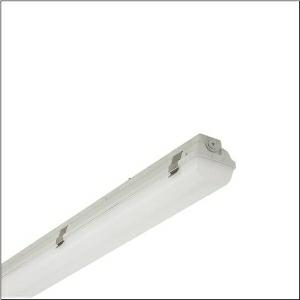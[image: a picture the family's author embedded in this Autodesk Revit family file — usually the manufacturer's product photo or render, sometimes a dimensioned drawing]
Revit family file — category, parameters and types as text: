
# Revit family: monsun_r__21_eco_51fj10dl45a_5ac6
name_source: partatom
category: Lighting Fixtures
units: mm (PartAtom-declared; Revit-internal decimal feet)

## family parameters
Cut with Voids When Loaded = No
Host = Face
Light Source = No
Part Type = Normal
Room Calculation Point = No
Round Connector Dimension = Use Diameter
Shared = No

## types (1)
- Monsun® 21 Eco (1 x LED, 5100 lm, 36 W, 4000K)
    Apparent Load = 36 VA
    CIE Flux Codes = 41 70 89 90 100
    Color Rendering = 80
    Color Temperature = 4000K
    Default Elevation = 1800 mm
    Description = Monsun® 21 Eco, damp-proof luminaire, primary optical cover: diffuser, of PMMA, frosted, light emission: direct distribution, primary light characteristic: symmetric, installation type: suspended mounting, surface-mounted, LED, rated luminous flux: 5.100lm, luminous efficacy: 142lm/W, light colour: 840, colour temperature: 4000K, control gear: ECG DALI, with terminal, 5-pole, max. 2.5mm², mains connection: 220..240V, AC, 50/60Hz, rated input power: 36W, housing, of glass-fibre reinforced polyester, light grey (RAL 7035), length: 1.277mm, width: 90mm, height: 95mm, clip for enclosure, of spring steel V2A, protection rating (complete): IP66, insulation class (complete): insulation class I (protective earthing), certification: CE, UKCA, protection symbol: D, impact resistance: IK02, permissible operating ambient temperature: -20..+35°C, corresponds to IFS (International Featured Standards) requirements for safety and quality in the food industry, packaging unit: 1 piece
    Height = 103 mm
    Lamp = 1 x LED
    Lamp Light Flux = 5100 lm
    Lamp Power = 36 W
    Lamp count = 1
    Length = 1277 mm
    Luminous efficacy = 142 lm/W
    Manufacturer = Siteco
    ModVariant = No
    Model = 51FJ10DL45A
    Mounting Place = Ceiling
    Mounting Type = Surface mounted
    Number of Poles = 1
    OnlyDefault = Yes
    Power Factor = 1
    Product Name = Monsun® 21 Eco
    Product group = damp-proof luminaire | ceiling mounted
    ProductGroupID = 300
    Protection Class = Protection class I
    Protection Degree = IP 66
    RLX_Detail_Level = 1
    RlxData = <blob elided: 33189 chars, md5=0796ca98>
    Socket = socket
    Standby Power = 0 W
    System Light Flux = 5100 lm
    System Power = 36 W
    Type Comments = Product without accessories
    Type Image = l_1007218.jpg
    URL = http://relux.com
    VarID = ---
    Voltage = 0 V
    Weight = 0.00 kg
    Width = 90 mm

## geometry (parser evidence)
native form markers: Blend x4, Sweep x12
no freeform markers — native parametric forms only
